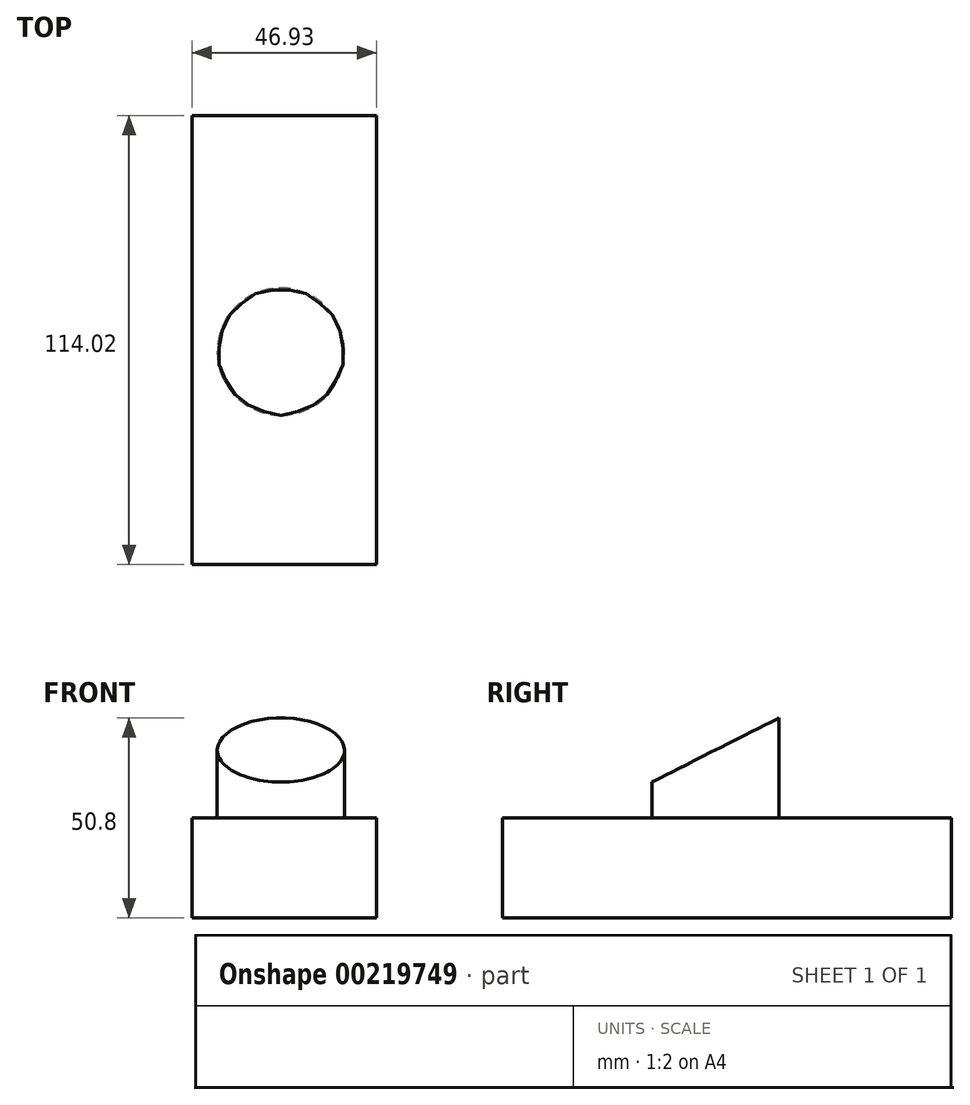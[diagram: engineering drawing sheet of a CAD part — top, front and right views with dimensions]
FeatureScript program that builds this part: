
annotation { "Feature Type Name" : "Feature", "Feature Type Description" : "" }
export const myFeature = defineFeature(function(context is Context, id is Id, definition is map)
    precondition{}
    {
        {
            var Q0;
            Q0=qCreatedBy(makeId("Top.planeOp"),FACE);
            var sketch = newSketch(context, id + "F0", { "sketchPlane" : qUnion([Q0])});
            skLineSegment(sketch, "E0.bottom", {"start": v(0, 52.32) * mm, "end": v(-46.93, 52.32) * mm});
            skLineSegment(sketch, "E0.top", {"start": v(0, -61.7) * mm, "end": v(-46.93, -61.7) * mm});
            skLineSegment(sketch, "E0.left", {"start": v(0, 52.32) * mm, "end": v(0, -61.7) * mm});
            skLineSegment(sketch, "E0.right", {"start": v(-46.93, 52.32) * mm, "end": v(-46.93, -61.7) * mm});
            skSolve(sketch);
        }
        {
            var Q0;
            Q0=makeQuery(id+"F0.imprint","IMPRINT",FACE,{"disambiguationData":[TD([[makeQuery(id+"F0.imprint","IMPRINT",EDGE,{"derivedFrom":sQuery(id+"F0.wireOp",EDGE,"E0.bottom")}),1.0]])]});
            extrude(context, id + "F1", {"entities" : qUnion([Q0]), "depth" : 25.4 * mm});
        }
        {
            var Q0;
            Q0=makeQuery(id+"F1.opExtrude","CAP_FACE",FACE,{"disambiguationData":[OSD([sQuery(id+"F0.wireOp",EDGE,"E0.bottom"),sQuery(id+"F0.wireOp",EDGE,"E0.top"),sQuery(id+"F0.wireOp",EDGE,"E0.left"),sQuery(id+"F0.wireOp",EDGE,"E0.right")])],"isStart":false});
            var sketch = newSketch(context, id + "F2", { "sketchPlane" : qUnion([Q0])});
            skCircle(sketch, "E1", {"center": v(-24.33, -7.63) * mm, "radius": 16.17 * mm});
            skSolve(sketch);
        }
        {
            var Q0;
            Q0 = qSketchRegion(id + "F2", true);
            extrude(context, id + "F3", {"entities" : qUnion([Q0]), "operationType" : NewBodyOperationType.ADD, "depth" : 25.4 * mm});
        }
        {
            var Q0;
            Q0=makeQuery(id+"F1.opExtrude","SWEPT_FACE",FACE,{"disambiguationData":[OSD([sQuery(id+"F0.wireOp",EDGE,"E0.right")])]});
            var sketch = newSketch(context, id + "F4", { "sketchPlane" : qUnion([Q0])});
            skLineSegment(sketch, "E2.0", {"start": v(-8.54, 50.8) * mm, "end": v(23.8, 50.8) * mm});
            skLineSegment(sketch, "E3", {"start": v(23.8, 50.8) * mm, "end": v(23.8, 25.4) * mm});
            skLineSegment(sketch, "E4", {"start": v(-8.54, 50.8) * mm, "end": v(23.8, 34.5) * mm});
            skSolve(sketch);
        }
        {
            var Q0;
            {var subQ0=sQuery(id+"F4.wireOp",EDGE,"E2.0");Q0=makeQuery(id+"F4.imprint","IMPRINT",FACE,{"disambiguationData":[TD([[makeQuery(id+"F4.imprint","IMPRINT",EDGE,{"derivedFrom":subQ0}),-1.0]])]});}
            extrude(context, id + "F5", {"entities" : qUnion([Q0]), "operationType" : NewBodyOperationType.REMOVE, "endBound" : BoundingType.THROUGH_ALL, "oppositeDirection" : true, "depth" : 25.4 * mm});
        }
    });
